# Revit family: Trägerklammer F9-M20
name_source: partatom
category: HLS-Bauteile
revit_build: Autodesk Revit 2017 (Build: 20190507_1515(x64)
units: mm (PartAtom-declared; Revit-internal decimal feet)

## family parameters
Arbeitsebenenbasiert = Ja
Beim Laden mit Abzugskörper schneiden = Nein
Bemaßung runder Anschluss = Durchmesser verwenden
Gemeinsam genutzt = Ja
Immer vertikal = Nein
Raumberechnungspunkt = Nein
Teiletyp = Normal

## types (1)
- Trägerklammer F9/M20
    Artikelnummer = 0579705
    Befestigung = mit Durchgangsloch
    EAN = 4250928414816
    Fabrikat = MEFA
    Firma = MEFA Befestigungs- und Montagesysteme GmbH
    Gewicht = 1.28 kg
    Gewicht pro Bauteil = 1.28 kg
    Gewinde = für M20
    Kurztext1 = Trägerklammer Guss F9
    Kurztext2 = Klemmbereich 32 - 82 mm Loch für M20
    Material = Temperguss
    Mengeneinheit = St
    Oberflaeche = galvanisch verzinkt
    Stärke = 25 mm  [stored 0.082021 ft]
    Vorgabe-Ansicht = 1219 mm
    max Klemmdicke = 82 mm  [stored 0.269029 ft]
    max. zul. Last = 8.40 kN
    min. Klemmdicke = 32 mm
    vpe = 1 St

note: [stored X ft] marks values corroborated as IEEE doubles in the binary element streams (Revit-internal decimal feet)
